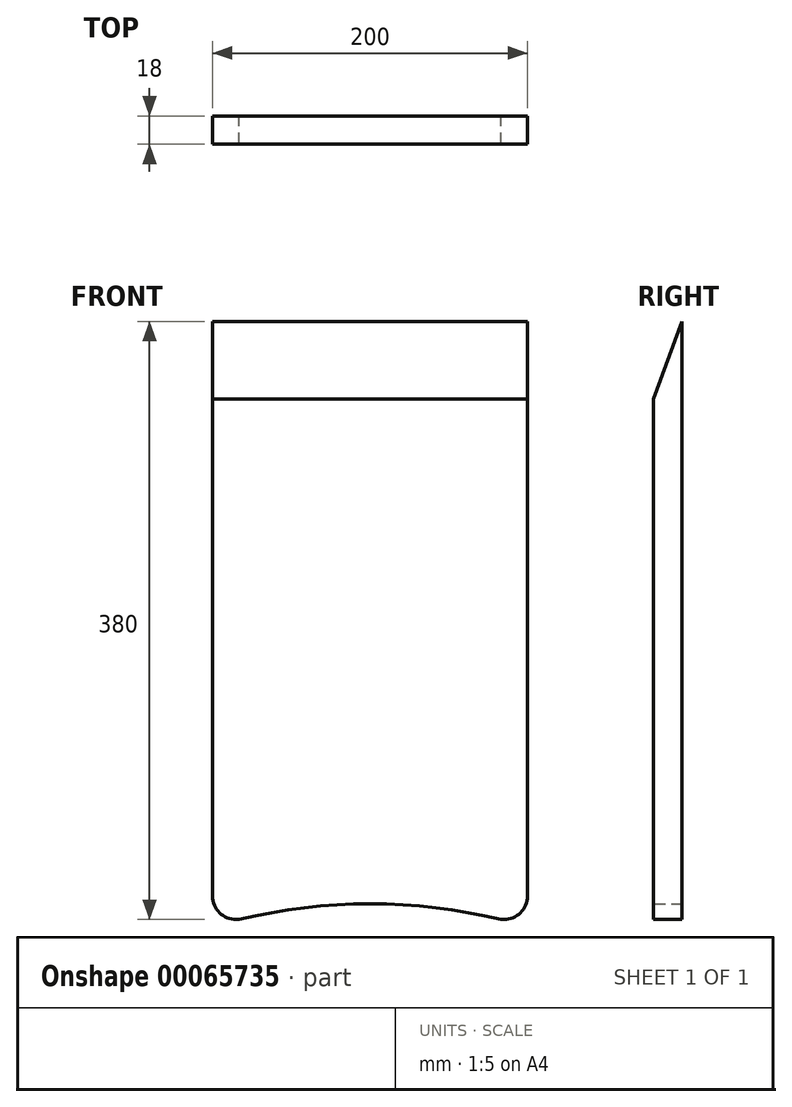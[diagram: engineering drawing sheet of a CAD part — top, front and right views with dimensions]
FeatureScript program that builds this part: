
annotation { "Feature Type Name" : "Feature", "Feature Type Description" : "" }
export const myFeature = defineFeature(function(context is Context, id is Id, definition is map)
    precondition{}
    {
        {
            var Q0;
            Q0=qCreatedBy(makeId("Front.planeOp"),FACE);
            var sketch = newSketch(context, id + "F0", { "sketchPlane" : qUnion([Q0])});
            skLineSegment(sketch, "E0.bottom", {"start": v(0, 0) * mm, "end": v(-200, 0) * mm});
            skLineSegment(sketch, "E0.top", {"start": v(0, -380) * mm, "end": v(-16.93, -380) * mm});
            skLineSegment(sketch, "E0.left", {"start": v(0, 0) * mm, "end": v(0, -380) * mm});
            skLineSegment(sketch, "E0.right", {"start": v(-200, 0) * mm, "end": v(-200, -380) * mm});
            skArc(sketch, "E1", {"start": v(-16.93, -380) * mm, "mid": v(-100, -370) * mm, "end": v(-183.07, -380) * mm});
            skLineSegment(sketch, "E2.trimOffspring", {"start": v(-183.07, -380) * mm, "end": v(-200, -380) * mm});
            skSolve(sketch);
        }
        {
            var Q0;
            Q0 = qSketchRegion(id + "F0", true);
            extrude(context, id + "F1", {"entities" : qUnion([Q0]), "depth" : 18 * mm});
        }
        {
            var Q0;
            Q0=makeQuery(id+"F1.opExtrude","SWEPT_FACE",FACE,{"disambiguationData":[OSD([sQuery(id+"F0.wireOp",EDGE,"E0.right")])]});
            var sketch = newSketch(context, id + "F2", { "sketchPlane" : qUnion([Q0])});
            skLineSegment(sketch, "E3.0", {"start": v(18, 0) * mm, "end": v(18, -49.45) * mm});
            skLineSegment(sketch, "E4.0", {"start": v(18, 0) * mm, "end": v(0, 0) * mm});
            skLineSegment(sketch, "E5", {"start": v(0, 0) * mm, "end": v(18, -49.45) * mm});
            skPoint(sketch, "E6.orphan", {"position": v(18, -380) * mm});
            skPoint(sketch, "E7.0.end.orphan", {"position": v(0, -380) * mm});
            skSolve(sketch);
        }
        {
            var Q0;
            Q0 = qSketchRegion(id + "F2", true);
            extrude(context, id + "F3", {"entities" : qUnion([Q0]), "operationType" : NewBodyOperationType.REMOVE, "endBound" : BoundingType.UP_TO_NEXT, "oppositeDirection" : true, "depth" : 25 * mm});
        }
        {
            var Q0;
            Q0=makeQuery(id+"F1.opExtrude","SWEPT_EDGE",EDGE,{"disambiguationData":[OSD([sQuery(id+"F0.wireOp",EDGE,"E0.right"),sQuery(id+"F0.wireOp",EDGE,"E2.trimOffspring")])]});
            var Q1;
            Q1=makeQuery(id+"F1.opExtrude","SWEPT_EDGE",EDGE,{"disambiguationData":[OSD([sQuery(id+"F0.wireOp",EDGE,"E0.top"),sQuery(id+"F0.wireOp",EDGE,"E0.left")])]});
            fillet(context, id + "F4", {"entities" : qUnion([Q0, Q1]), "radius" : 15 * mm, "tangentPropagation" : true, "allowEdgeOverflow" : false});
        }
    });
